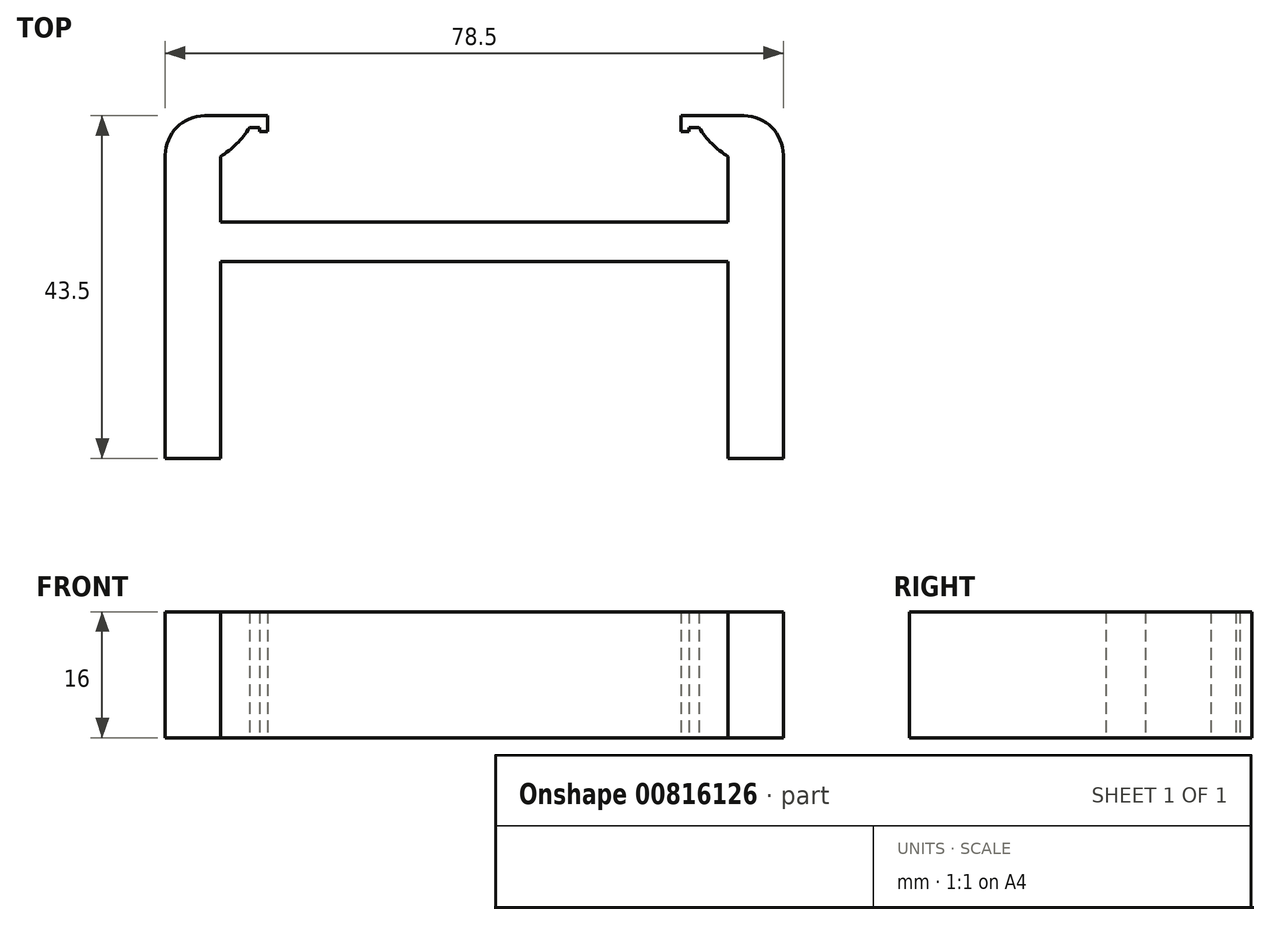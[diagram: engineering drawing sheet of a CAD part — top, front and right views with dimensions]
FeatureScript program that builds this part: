
annotation { "Feature Type Name" : "Feature", "Feature Type Description" : "" }
export const myFeature = defineFeature(function(context is Context, id is Id, definition is map)
    precondition{}
    {
        {
            var Q0;
            Q0=qCreatedBy(makeId("Top.planeOp"),FACE);
            var sketch = newSketch(context, id + "F0", { "sketchPlane" : qUnion([Q0])});
            skLineSegment(sketch, "E0.bottom", {"start": v(32.25, 2.5) * mm, "end": v(-32.25, 2.5) * mm});
            skLineSegment(sketch, "E0.top", {"start": v(32.25, -2.5) * mm, "end": v(-32.25, -2.5) * mm});
            skLineSegment(sketch, "E0.left", {"start": v(32.25, 2.5) * mm, "end": v(32.25, -2.5) * mm});
            skLineSegment(sketch, "E0.right", {"start": v(-32.25, 2.5) * mm, "end": v(-32.25, -2.5) * mm});
            skPoint(sketch, "E0.middle", {"position": v(0, 0) * mm});
            skLineSegment(sketch, "E1.bottom", {"start": v(-32.25, 2.5) * mm, "end": v(-39.25, 2.5) * mm});
            skLineSegment(sketch, "E1.top", {"start": v(-32.25, 14.5) * mm, "end": v(-39.25, 14.5) * mm});
            skLineSegment(sketch, "E1.left", {"start": v(-32.25, 2.5) * mm, "end": v(-32.25, 14.5) * mm});
            skLineSegment(sketch, "E1.right", {"start": v(-39.25, 2.5) * mm, "end": v(-39.25, 14.5) * mm});
            skLineSegment(sketch, "E2.top", {"start": v(-32.25, -27.5) * mm, "end": v(-39.25, -27.5) * mm});
            skLineSegment(sketch, "E2.left", {"start": v(-32.25, 2.5) * mm, "end": v(-32.25, -27.5) * mm});
            skLineSegment(sketch, "E2.right", {"start": v(-39.25, 2.5) * mm, "end": v(-39.25, -27.5) * mm});
            skLineSegment(sketch, "E3.bottom", {"start": v(32.25, 14.5) * mm, "end": v(39.25, 14.5) * mm});
            skLineSegment(sketch, "E3.top", {"start": v(32.25, -27.5) * mm, "end": v(39.25, -27.5) * mm});
            skLineSegment(sketch, "E3.left", {"start": v(32.25, 14.5) * mm, "end": v(32.25, -27.5) * mm});
            skLineSegment(sketch, "E3.right", {"start": v(39.25, 14.5) * mm, "end": v(39.25, -27.5) * mm});
            skLineSegment(sketch, "E4.bottom", {"start": v(-32.25, 2.5) * mm, "end": v(-28.25, 2.5) * mm});
            skLineSegment(sketch, "E4.top", {"start": v(-32.25, 14.5) * mm, "end": v(-28.25, 14.5) * mm});
            skLineSegment(sketch, "E4.right", {"start": v(-28.25, 2.5) * mm, "end": v(-28.25, 14.5) * mm});
            skLineSegment(sketch, "E5.bottom", {"start": v(32.25, 2.5) * mm, "end": v(28.25, 2.5) * mm});
            skLineSegment(sketch, "E5.top", {"start": v(32.25, 14.5) * mm, "end": v(28.25, 14.5) * mm});
            skLineSegment(sketch, "E5.left", {"start": v(32.25, 2.5) * mm, "end": v(32.25, 14.5) * mm});
            skLineSegment(sketch, "E5.right", {"start": v(28.25, 2.5) * mm, "end": v(28.25, 14.5) * mm});
            skLineSegment(sketch, "E6.bottom", {"start": v(-28.25, 14.5) * mm, "end": v(-32.25, 14.5) * mm});
            skLineSegment(sketch, "E6.top", {"start": v(-28.25, 10.5) * mm, "end": v(-32.25, 10.5) * mm});
            skLineSegment(sketch, "E6.left", {"start": v(-28.25, 14.5) * mm, "end": v(-28.25, 10.5) * mm});
            skLineSegment(sketch, "E6.right", {"start": v(-32.25, 14.5) * mm, "end": v(-32.25, 10.5) * mm});
            skLineSegment(sketch, "E7", {"start": v(-28.25, 14.5) * mm, "end": v(-32.25, 10.5) * mm});
            skLineSegment(sketch, "E8.bottom", {"start": v(-32.25, 14.5) * mm, "end": v(-28.55, 14.5) * mm});
            skLineSegment(sketch, "E8.top", {"start": v(-32.25, 10.8) * mm, "end": v(-28.55, 10.8) * mm});
            skLineSegment(sketch, "E8.left", {"start": v(-32.25, 14.5) * mm, "end": v(-32.25, 10.8) * mm});
            skLineSegment(sketch, "E8.right", {"start": v(-28.55, 14.5) * mm, "end": v(-28.55, 10.8) * mm});
            skArc(sketch, "E9", {"start": v(-32.25, 10.8) * mm, "mid": v(-30.2, 12.45) * mm, "end": v(-28.55, 14.5) * mm});
            skLineSegment(sketch, "E10.bottom", {"start": v(32.25, 14.5) * mm, "end": v(28.55, 14.5) * mm});
            skLineSegment(sketch, "E10.top", {"start": v(32.25, 10.8) * mm, "end": v(28.55, 10.8) * mm});
            skLineSegment(sketch, "E10.left", {"start": v(32.25, 14.5) * mm, "end": v(32.25, 10.8) * mm});
            skLineSegment(sketch, "E10.right", {"start": v(28.55, 14.5) * mm, "end": v(28.55, 10.8) * mm});
            skArc(sketch, "E11", {"start": v(28.55, 14.5) * mm, "mid": v(30.2, 12.45) * mm, "end": v(32.25, 10.8) * mm});
            skLineSegment(sketch, "E12.bottom", {"start": v(39.25, 14.5) * mm, "end": v(26.25, 14.5) * mm});
            skLineSegment(sketch, "E12.top", {"start": v(39.25, 16) * mm, "end": v(26.25, 16) * mm});
            skLineSegment(sketch, "E12.left", {"start": v(39.25, 14.5) * mm, "end": v(39.25, 16) * mm});
            skLineSegment(sketch, "E12.right", {"start": v(26.25, 14.5) * mm, "end": v(26.25, 16) * mm});
            skLineSegment(sketch, "E13.bottom", {"start": v(26.25, 14.5) * mm, "end": v(27.25, 14.5) * mm});
            skLineSegment(sketch, "E13.top", {"start": v(26.25, 14) * mm, "end": v(27.25, 14) * mm});
            skLineSegment(sketch, "E13.left", {"start": v(26.25, 14.5) * mm, "end": v(26.25, 14) * mm});
            skLineSegment(sketch, "E13.right", {"start": v(27.25, 14.5) * mm, "end": v(27.25, 14) * mm});
            skLineSegment(sketch, "E14.bottom", {"start": v(-39.25, 14.5) * mm, "end": v(-26.25, 14.5) * mm});
            skLineSegment(sketch, "E14.top", {"start": v(-39.25, 16) * mm, "end": v(-26.25, 16) * mm});
            skLineSegment(sketch, "E14.left", {"start": v(-39.25, 14.5) * mm, "end": v(-39.25, 16) * mm});
            skLineSegment(sketch, "E14.right", {"start": v(-26.25, 14.5) * mm, "end": v(-26.25, 16) * mm});
            skLineSegment(sketch, "E15.bottom", {"start": v(-26.25, 14.5) * mm, "end": v(-27.25, 14.5) * mm});
            skLineSegment(sketch, "E15.top", {"start": v(-26.25, 14) * mm, "end": v(-27.25, 14) * mm});
            skLineSegment(sketch, "E15.left", {"start": v(-26.25, 14.5) * mm, "end": v(-26.25, 14) * mm});
            skLineSegment(sketch, "E15.right", {"start": v(-27.25, 14.5) * mm, "end": v(-27.25, 14) * mm});
            skSolve(sketch);
        }
        {
            var Q0;
            Q0=makeQuery(id+"F0.imprint","IMPRINT",FACE,{"disambiguationData":[TD([[makeQuery(id+"F0.imprint","IMPRINT",EDGE,{"derivedFrom":sQuery(id+"F0.wireOp",EDGE,"E0.top")}),-1.0]])]});
            var Q1;
            Q1=makeQuery(id+"F0.imprint","IMPRINT",FACE,{"disambiguationData":[TD([[makeQuery(id+"F0.imprint","IMPRINT",EDGE,{"derivedFrom":sQuery(id+"F0.wireOp",EDGE,"E0.right")}),-1.0]])]});
            var Q2;
            Q2=makeQuery(id+"F0.imprint","IMPRINT",FACE,{"disambiguationData":[TD([[makeQuery(id+"F0.imprint","IMPRINT",EDGE,{"derivedFrom":sQuery(id+"F0.wireOp",EDGE,"E1.top")}),1.0]])]});
            var Q3;
            {var subQ4=sQuery(id+"F0.wireOp",EDGE,"E8.bottom");Q3=makeQuery(id+"F0.imprint","IMPRINT",FACE,{"disambiguationData":[TD([[makeQuery(id+"F0.imprint","IMPRINT",EDGE,{"derivedFrom":subQ4}),-1.0]])]});}
            var Q4;
            Q4=makeQuery(id+"F0.imprint","IMPRINT",FACE,{"disambiguationData":[TD([[makeQuery(id+"F0.imprint","IMPRINT",EDGE,{"derivedFrom":sQuery(id+"F0.wireOp",EDGE,"E10.bottom")}),1.0]])]});
            var Q5;
            Q5=makeQuery(id+"F0.imprint","IMPRINT",FACE,{"disambiguationData":[TD([[makeQuery(id+"F0.imprint","IMPRINT",EDGE,{"derivedFrom":sQuery(id+"F0.wireOp",EDGE,"E3.bottom")}),-1.0]])]});
            var Q6;
            {var subQ0=sQuery(id+"F0.wireOp",EDGE,"E9");var subQ1=sQuery(id+"F0.wireOp",EDGE,"E7");var subQ2=makeQuery(id+"F0.imprint","INTERSECT",VERTEX,{"disambiguationData":[OD(0.0)],"derivedFrom":[subQ1,subQ0]});Q6=makeQuery(id+"F0.imprint","IMPRINT",FACE,{"disambiguationData":[TD([[makeQuery(id+"F0.imprint","IMPRINT",EDGE,{"disambiguationData":[TD([[subQ2,-1.0]])],"derivedFrom":subQ1}),1.0]])]});}
            var Q7;
            {var subQ3=sQuery(id+"F0.wireOp",EDGE,"E1.bottom");Q7=makeQuery(id+"F0.imprint","IMPRINT",FACE,{"disambiguationData":[TD([[makeQuery(id+"F0.imprint","IMPRINT",EDGE,{"derivedFrom":subQ3}),-1.0]])]});}
            var Q8;
            {var subQ0=sQuery(id+"F0.wireOp",EDGE,"E9");var subQ3=sQuery(id+"F0.wireOp",EDGE,"E7");var subQ8=makeQuery(id+"F0.imprint","INTERSECT",VERTEX,{"disambiguationData":[OD(0.0)],"derivedFrom":[subQ3,subQ0]});Q8=makeQuery(id+"F0.imprint","IMPRINT",FACE,{"disambiguationData":[TD([[makeQuery(id+"F0.imprint","IMPRINT",EDGE,{"disambiguationData":[TD([[subQ8,-1.0]])],"derivedFrom":subQ3}),-1.0]])]});}
            var Q9;
            {var subQ1=sQuery(id+"F0.wireOp",EDGE,"E1.top");Q9=makeQuery(id+"F0.imprint","IMPRINT",FACE,{"disambiguationData":[TD([[makeQuery(id+"F0.imprint","IMPRINT",EDGE,{"derivedFrom":subQ1}),-1.0]])]});}
            var Q10;
            Q10=makeQuery(id+"F0.imprint","IMPRINT",FACE,{"disambiguationData":[TD([[makeQuery(id+"F0.imprint","IMPRINT",EDGE,{"derivedFrom":sQuery(id+"F0.wireOp",EDGE,"E15.top")}),-1.0]])]});
            var Q11;
            {var subQ3=sQuery(id+"F0.wireOp",EDGE,"E11");Q11=makeQuery(id+"F0.imprint","IMPRINT",FACE,{"disambiguationData":[TD([[makeQuery(id+"F0.imprint","IMPRINT",EDGE,{"derivedFrom":subQ3}),1.0]])]});}
            var Q12;
            {var subQ1=sQuery(id+"F0.wireOp",EDGE,"E0.left");Q12=makeQuery(id+"F0.imprint","IMPRINT",FACE,{"disambiguationData":[TD([[makeQuery(id+"F0.imprint","IMPRINT",EDGE,{"derivedFrom":subQ1}),1.0]])]});}
            var Q13;
            {var subQ6=sQuery(id+"F0.wireOp",EDGE,"E3.bottom");Q13=makeQuery(id+"F0.imprint","IMPRINT",FACE,{"disambiguationData":[TD([[makeQuery(id+"F0.imprint","IMPRINT",EDGE,{"derivedFrom":subQ6}),1.0]])]});}
            var Q14;
            Q14=makeQuery(id+"F0.imprint","IMPRINT",FACE,{"disambiguationData":[TD([[makeQuery(id+"F0.imprint","IMPRINT",EDGE,{"derivedFrom":sQuery(id+"F0.wireOp",EDGE,"E13.top")}),1.0]])]});
            extrude(context, id + "F1", {"entities" : qUnion([Q0, Q1, Q2, Q3, Q4, Q5, Q6, Q7, Q8, Q9, Q10, Q11, Q12, Q13, Q14]), "depth" : 16 * mm, "offsetDistance" : 25 * mm});
        }
        {
            var Q0;
            Q0=makeQuery(id+"F1.opExtrude","SWEPT_EDGE",EDGE,{"disambiguationData":[OSD([sQuery(id+"F0.wireOp",EDGE,"E14.top"),sQuery(id+"F0.wireOp",EDGE,"E14.left")])]});
            var Q1;
            Q1=makeQuery(id+"F1.opExtrude","SWEPT_EDGE",EDGE,{"disambiguationData":[OSD([sQuery(id+"F0.wireOp",EDGE,"E12.top"),sQuery(id+"F0.wireOp",EDGE,"E12.left")])]});
            fillet(context, id + "F2", {"entities" : qUnion([Q0, Q1]), "radius" : 5 * mm, "tangentPropagation" : true, "allowEdgeOverflow" : false});
        }
    });
